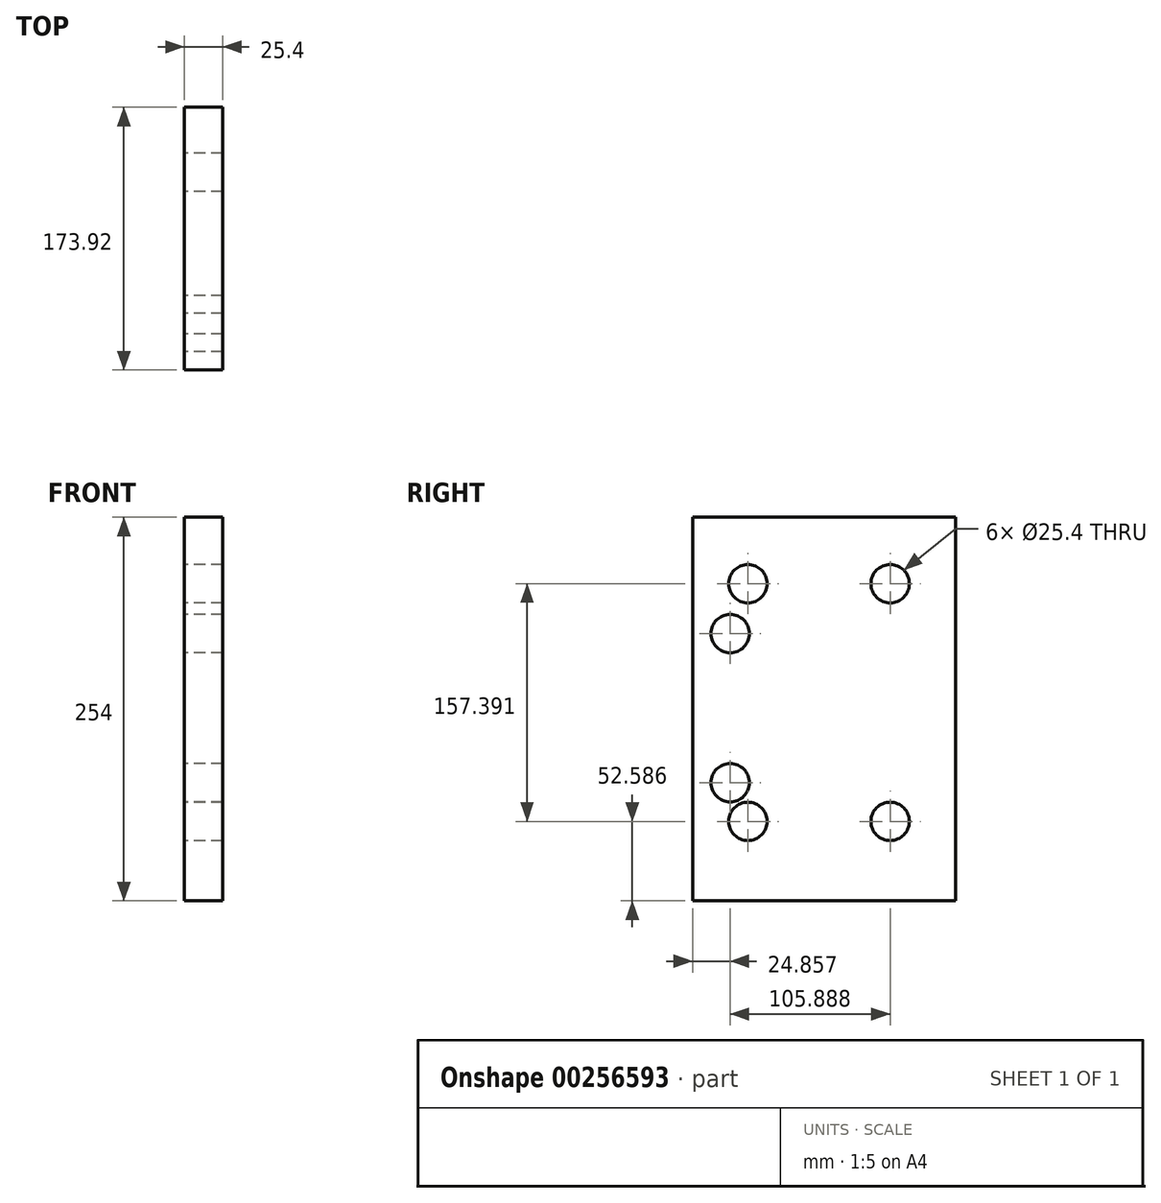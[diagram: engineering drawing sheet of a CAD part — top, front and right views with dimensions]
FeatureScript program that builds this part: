
annotation { "Feature Type Name" : "Feature", "Feature Type Description" : "" }
export const myFeature = defineFeature(function(context is Context, id is Id, definition is map)
    precondition{}
    {
        {
            var Q0;
            Q0=qCreatedBy(makeId("Right.planeOp"),FACE);
            var sketch = newSketch(context, id + "F0", { "sketchPlane" : qUnion([Q0])});
            skLineSegment(sketch, "E0.bottom", {"start": v(64.7, -134.03) * mm, "end": v(-109.23, -134.03) * mm});
            skLineSegment(sketch, "E0.top", {"start": v(64.7, 119.97) * mm, "end": v(-109.23, 119.97) * mm});
            skLineSegment(sketch, "E0.left", {"start": v(64.7, -134.03) * mm, "end": v(64.7, 119.97) * mm});
            skLineSegment(sketch, "E0.right", {"start": v(-109.23, -134.03) * mm, "end": v(-109.23, 119.97) * mm});
            skSolve(sketch);
        }
        {
            var Q0;
            Q0 = qSketchRegion(id + "F0", true);
            extrude(context, id + "F1", {"entities" : qUnion([Q0]), "depth" : 25.4 * mm});
        }
        {
            var Q0;
            Q0=makeQuery(id+"F1.opExtrude","CAP_FACE",FACE,{"disambiguationData":[OSD([sQuery(id+"F0.wireOp",EDGE,"E0.bottom"),sQuery(id+"F0.wireOp",EDGE,"E0.top"),sQuery(id+"F0.wireOp",EDGE,"E0.left"),sQuery(id+"F0.wireOp",EDGE,"E0.right")])],"isStart":true});
            var sketch = newSketch(context, id + "F2", { "sketchPlane" : qUnion([Q0])});
            skLineSegment(sketch, "E1.bottom", {"start": v(-21.51, 75.95) * mm, "end": v(72.65, 75.95) * mm});
            skLineSegment(sketch, "E1.top", {"start": v(-21.51, -81.44) * mm, "end": v(72.65, -81.44) * mm});
            skLineSegment(sketch, "E1.left", {"start": v(-21.51, 75.95) * mm, "end": v(-21.51, -81.44) * mm});
            skLineSegment(sketch, "E1.right", {"start": v(72.65, 75.95) * mm, "end": v(72.65, -81.44) * mm});
            skSolve(sketch);
        }
        {
            var Q0;
            Q0=sQuery(id+"F2.wireOp",VERTEX,"E1.left.end");
            var Q1;
            Q1=sQuery(id+"F2.wireOp",VERTEX,"E1.top.end");
            var Q2;
            Q2=sQuery(id+"F2.wireOp",VERTEX,"E1.left.start");
            var Q3;
            Q3=sQuery(id+"F2.wireOp",VERTEX,"E1.bottom.end");
            var Q4;
            Q4=makeQuery(id+"F1.opExtrude","SWEPT_BODY",BODY,{"disambiguationData":[OSD([sQuery(id+"F0.wireOp",EDGE,"E0.bottom"),sQuery(id+"F0.wireOp",EDGE,"E0.top"),sQuery(id+"F0.wireOp",EDGE,"E0.left"),sQuery(id+"F0.wireOp",EDGE,"E0.right")])]});
            hole(context, id + "F3", {"style" : HoleStyle.SIMPLE, "endStyle" : HoleEndStyle.THROUGH, "holeDiameter" : 25.4 * mm, "tappedDepth" : 12.7 * mm, "tapClearance" : 3, "locations" : qUnion([Q0, Q1, Q2, Q3]), "scope" : qUnion([Q4])});
        }
        {
            var Q0;
            Q0=makeQuery(id+"F1.opExtrude","CAP_FACE",FACE,{"disambiguationData":[OSD([sQuery(id+"F0.wireOp",EDGE,"E0.bottom"),sQuery(id+"F0.wireOp",EDGE,"E0.top"),sQuery(id+"F0.wireOp",EDGE,"E0.left"),sQuery(id+"F0.wireOp",EDGE,"E0.right")])],"isStart":true});
            var sketch = newSketch(context, id + "F4", { "sketchPlane" : qUnion([Q0])});
            skLineSegment(sketch, "E2.bottom", {"start": v(95.97, 42.94) * mm, "end": v(84.37, 42.94) * mm});
            skLineSegment(sketch, "E2.top", {"start": v(95.97, -55.82) * mm, "end": v(84.37, -55.82) * mm});
            skLineSegment(sketch, "E2.left", {"start": v(95.97, 42.94) * mm, "end": v(95.97, -55.82) * mm});
            skLineSegment(sketch, "E2.right", {"start": v(84.37, 42.94) * mm, "end": v(84.37, -55.82) * mm});
            skSolve(sketch);
        }
        {
            var Q0;
            Q0=sQuery(id+"F4.wireOp",VERTEX,"E2.right.end");
            var Q1;
            Q1=sQuery(id+"F4.wireOp",VERTEX,"E2.right.start");
            var Q2;
            Q2=makeQuery(id+"F1.opExtrude","SWEPT_BODY",BODY,{"disambiguationData":[OSD([sQuery(id+"F0.wireOp",EDGE,"E0.bottom"),sQuery(id+"F0.wireOp",EDGE,"E0.top"),sQuery(id+"F0.wireOp",EDGE,"E0.left"),sQuery(id+"F0.wireOp",EDGE,"E0.right")])]});
            hole(context, id + "F5", {"style" : HoleStyle.SIMPLE, "endStyle" : HoleEndStyle.THROUGH, "holeDiameter" : 25.4 * mm, "tappedDepth" : 12.7 * mm, "tapClearance" : 3, "locations" : qUnion([Q0, Q1]), "scope" : qUnion([Q2])});
        }
    });
